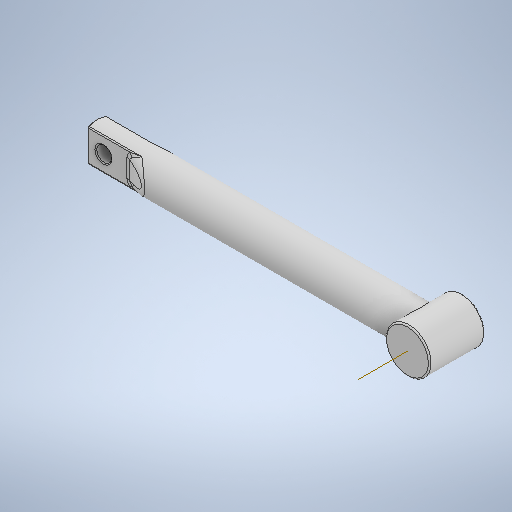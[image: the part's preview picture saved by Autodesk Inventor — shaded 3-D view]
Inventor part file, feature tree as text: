
AUTODESK INVENTOR PART (.ipt)
format: ipt  version: 2025.1 (Build 291241000, 241)  size: 400,896 bytes
history: native  units: mm
features: fillet x4, sketch x4, extrude x3, chamfer x2, revolve x1, other x1
ambient origin geometry x8: Origin, YZ Plane, XZ Plane, XY Plane, X Axis, Y Axis, Z Axis, Center Point
bodies: Volumenkörper1 (feature_tree)
feature tree (15):
  revolve  "Umdrehung1"
  extrude  "Extrusion1"  Depth=4.0mm
  extrude  "Extrusion2"  Depth=35.0mm
  fillet  "Rundung5"  [1 undecoded]
  extrude  "Extrusion3"  Depth=12.0mm TaperAngle=0.0deg
  chamfer  "Fasen1"  Distance=12.0mm
  chamfer  "Fasen2"  Distance=0.3mm
  fillet  "Rundung9"  Radius=14.0mm
  fillet  "Rundung10"  Radius=9.0mm
  fillet  "Rundung11"  [1 undecoded]
  other  "Arbeitsachse1"
  sketch  "Skizze1"  dims[d0=73.5mm d1=4.0mm]
  sketch  "Skizze2"  dims[d2=0.0mm d3=35.0mm d4=90.0deg]
  sketch  "Skizze4"  dims[d5=9.7mm d6=12.0mm d7=0.0mm]
  sketch  "Skizze6"  dims[d15=2.0mm d16=12.0mm d17=5.0mm d18=0.0mm d19=0.0mm d24=0.3mm d31=14.0mm d33=9.0mm d36=0.0mm d39=3.3mm d40=0.0mm d41=70.0mm d42=6.0mm d43=0.0mm d44=0.2mm d45=2.0mm d46=45.0deg d47=0.2mm d48=2.0mm d49=45.0deg d50=2.0mm d51=0.3mm d52=2.0mm d20=0.0mm d21=0.0mm d22=0.0mm d23=0.0mm]
note: 2 required parameter values undecoded (feature->parameter linkage not recoverable at this tier; creation-order binding heuristic only, values carry confidence <= 0.55)
